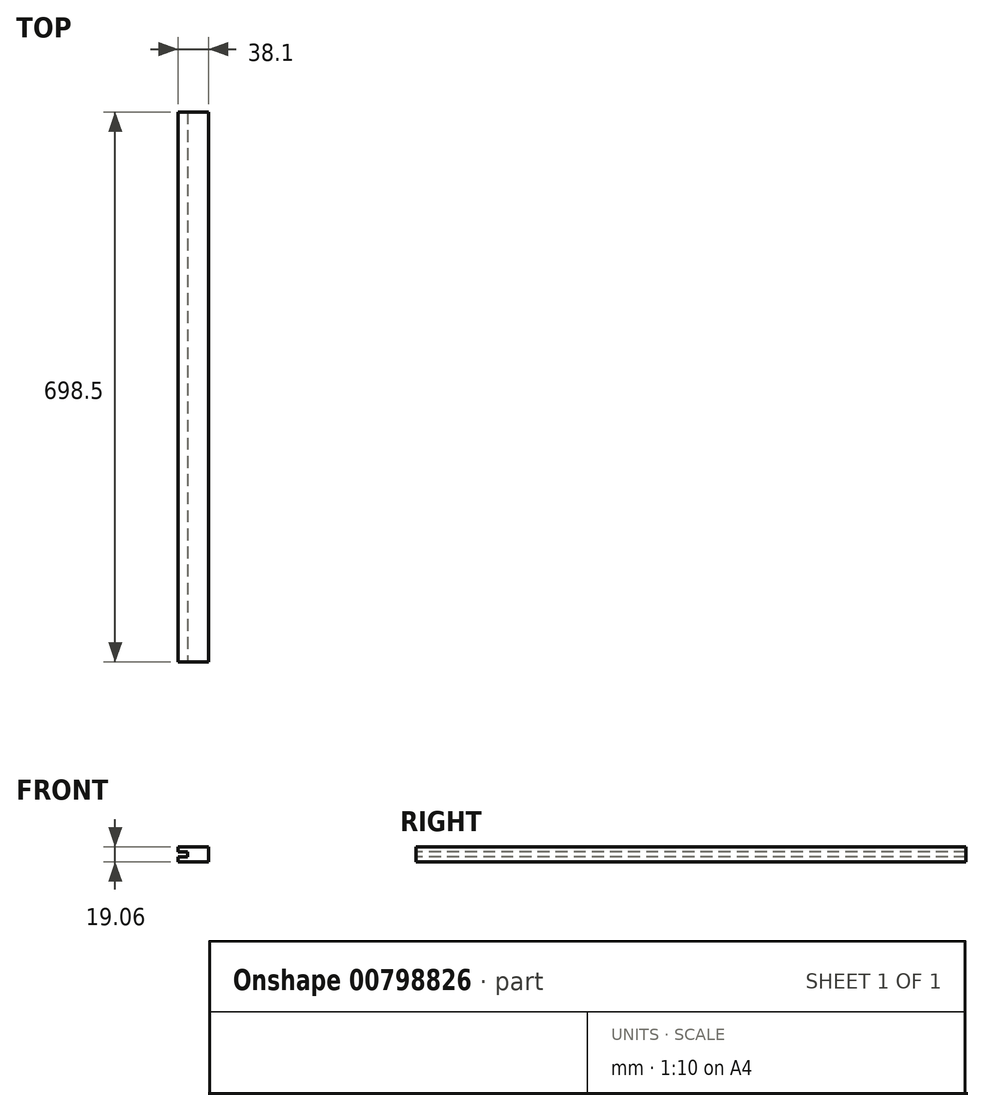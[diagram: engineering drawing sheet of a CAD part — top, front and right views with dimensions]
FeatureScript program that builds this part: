
annotation { "Feature Type Name" : "Feature", "Feature Type Description" : "" }
export const myFeature = defineFeature(function(context is Context, id is Id, definition is map)
    precondition{}
    {
        {
            var Q0;
            Q0=qCreatedBy(makeId("Front.planeOp"),FACE);
            var sketch = newSketch(context, id + "F0", { "sketchPlane" : qUnion([Q0])});
            skLineSegment(sketch, "E0.bottom", {"start": v(-19.05, 9.52) * mm, "end": v(19.05, 9.52) * mm});
            skLineSegment(sketch, "E0.top", {"start": v(-19.05, -9.53) * mm, "end": v(19.05, -9.53) * mm});
            skLineSegment(sketch, "E0.left", {"start": v(-19.05, 9.52) * mm, "end": v(-19.05, -9.53) * mm});
            skLineSegment(sketch, "E0.right", {"start": v(19.05, 9.53) * mm, "end": v(19.05, -9.52) * mm});
            skSolve(sketch);
        }
        {
            var Q0;
            Q0=makeQuery(id+"F0.imprint","IMPRINT",FACE,{"disambiguationData":[TD([[makeQuery(id+"F0.imprint","IMPRINT",EDGE,{"derivedFrom":sQuery(id+"F0.wireOp",EDGE,"E0.bottom")}),-1.0]])]});
            extrude(context, id + "F1", {"entities" : qUnion([Q0]), "depth" : 698.5 * mm, "offsetDistance" : 25.4 * mm});
        }
        {
            var Q0;
            Q0=makeQuery(id+"F1.opExtrude","CAP_FACE",FACE,{"disambiguationData":[OSD([sQuery(id+"F0.wireOp",EDGE,"E0.bottom"),sQuery(id+"F0.wireOp",EDGE,"E0.top"),sQuery(id+"F0.wireOp",EDGE,"E0.left"),sQuery(id+"F0.wireOp",EDGE,"E0.right")])],"isStart":false});
            var sketch = newSketch(context, id + "F2", { "sketchPlane" : qUnion([Q0])});
            skLineSegment(sketch, "E1.bottom", {"start": v(-19.05, -3.18) * mm, "end": v(-7.57, -3.18) * mm});
            skLineSegment(sketch, "E1.top", {"start": v(-19.05, 3.17) * mm, "end": v(-7.57, 3.17) * mm});
            skLineSegment(sketch, "E1.left", {"start": v(-19.05, -3.18) * mm, "end": v(-19.05, 3.17) * mm});
            skLineSegment(sketch, "E1.right", {"start": v(-7.57, -3.18) * mm, "end": v(-7.57, 3.17) * mm});
            skLineSegment(sketch, "E2.bottom", {"start": v(-19.05, 0) * mm, "end": v(-19.05, 0) * mm});
            skLineSegment(sketch, "E2.top", {"start": v(-19.05, -4.65) * mm, "end": v(-19.05, -4.65) * mm});
            skLineSegment(sketch, "E2.left", {"start": v(-19.05, 0) * mm, "end": v(-19.05, -4.65) * mm});
            skLineSegment(sketch, "E2.right", {"start": v(-19.05, 0) * mm, "end": v(-19.05, -4.65) * mm});
            skSolve(sketch);
        }
        {
            var Q0;
            Q0 = qSketchRegion(id + "F2", true);
            extrude(context, id + "F3", {"entities" : qUnion([Q0]), "operationType" : NewBodyOperationType.REMOVE, "endBound" : BoundingType.THROUGH_ALL, "oppositeDirection" : true, "depth" : 25.4 * mm, "offsetDistance" : 25.4 * mm});
        }
    });
